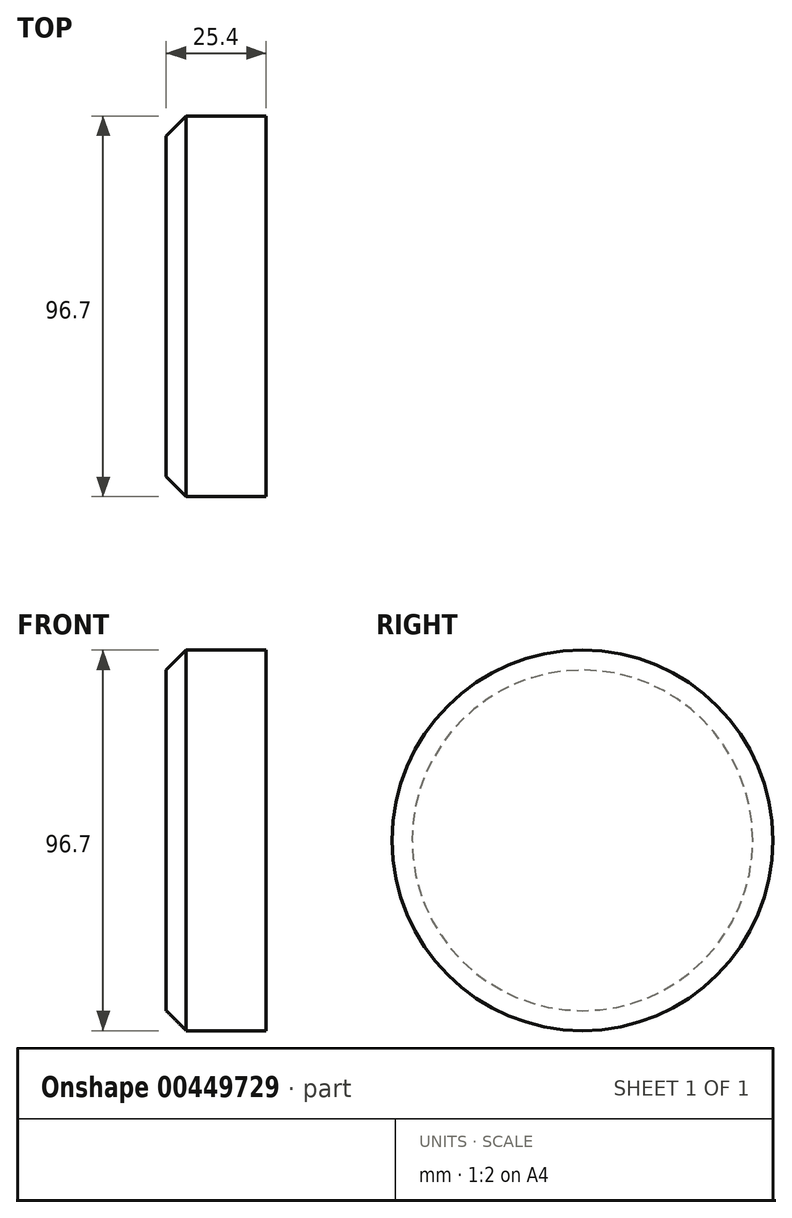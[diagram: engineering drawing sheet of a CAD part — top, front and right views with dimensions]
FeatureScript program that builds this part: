
annotation { "Feature Type Name" : "Feature", "Feature Type Description" : "" }
export const myFeature = defineFeature(function(context is Context, id is Id, definition is map)
    precondition{}
    {
        {
            var Q0;
            Q0=qCreatedBy(makeId("Right.planeOp"),FACE);
            var sketch = newSketch(context, id + "F0", { "sketchPlane" : qUnion([Q0])});
            skCircle(sketch, "E0", {"center": v(0, 0) * mm, "radius": 48.35 * mm});
            skSolve(sketch);
        }
        {
            var Q0;
            Q0=makeQuery(id+"F0.imprint","IMPRINT",FACE,{"disambiguationData":[TD([[makeQuery(id+"F0.imprint","IMPRINT",EDGE,{"derivedFrom":sQuery(id+"F0.wireOp",EDGE,"E0")}),1.0]])]});
            extrude(context, id + "F1", {"entities" : qUnion([Q0]), "depth" : 25.4 * mm});
        }
        {
            var Q0;
            Q0=makeQuery(id+"F1.opExtrude","CAP_FACE",FACE,{"disambiguationData":[OSD([sQuery(id+"F0.wireOp",EDGE,"E0")])],"isStart":true});
            chamfer(context, id + "F2", {"entities" : qUnion([Q0]), "width" : 5.08 * mm, "tangentPropagation" : true});
        }
    });
